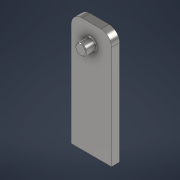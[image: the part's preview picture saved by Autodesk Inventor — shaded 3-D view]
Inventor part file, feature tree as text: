
AUTODESK INVENTOR PART (.ipt)
format: ipt  version: 2021 (Build 250183000, 183)  size: 271,360 bytes
history: native  units: mm
features: extrude x2, fillet x2, sketch x2, chamfer x1
ambient origin geometry x8: Origin, YZ Plane, XZ Plane, XY Plane, X Axis, Y Axis, Z Axis, Center Point
bodies: Solid1 (feature_tree)
feature tree (7):
  extrude  "Extrusion1"  Depth=85.0mm
  fillet  "Fillet1"  Radius=15.0mm
  extrude  "Extrusion2"  Depth=6.0mm TaperAngle=0.0deg
  fillet  "Fillet2"  Radius=8.0mm
  chamfer  "Chamfer1"  Distance=72.0mm
  sketch  "Sketch1"  dims[d0=30.0mm d1=85.0mm d2=15.0mm]
  sketch  "Sketch2"  dims[d3=85.0mm d4=6.0mm d5=0.0mm d6=8.0mm d7=72.0mm d8=8.0mm d9=8.0mm d10=0.0mm d11=1.0mm d12=0.0mm d13=0.5mm d14=2.0mm d15=45.0deg]
